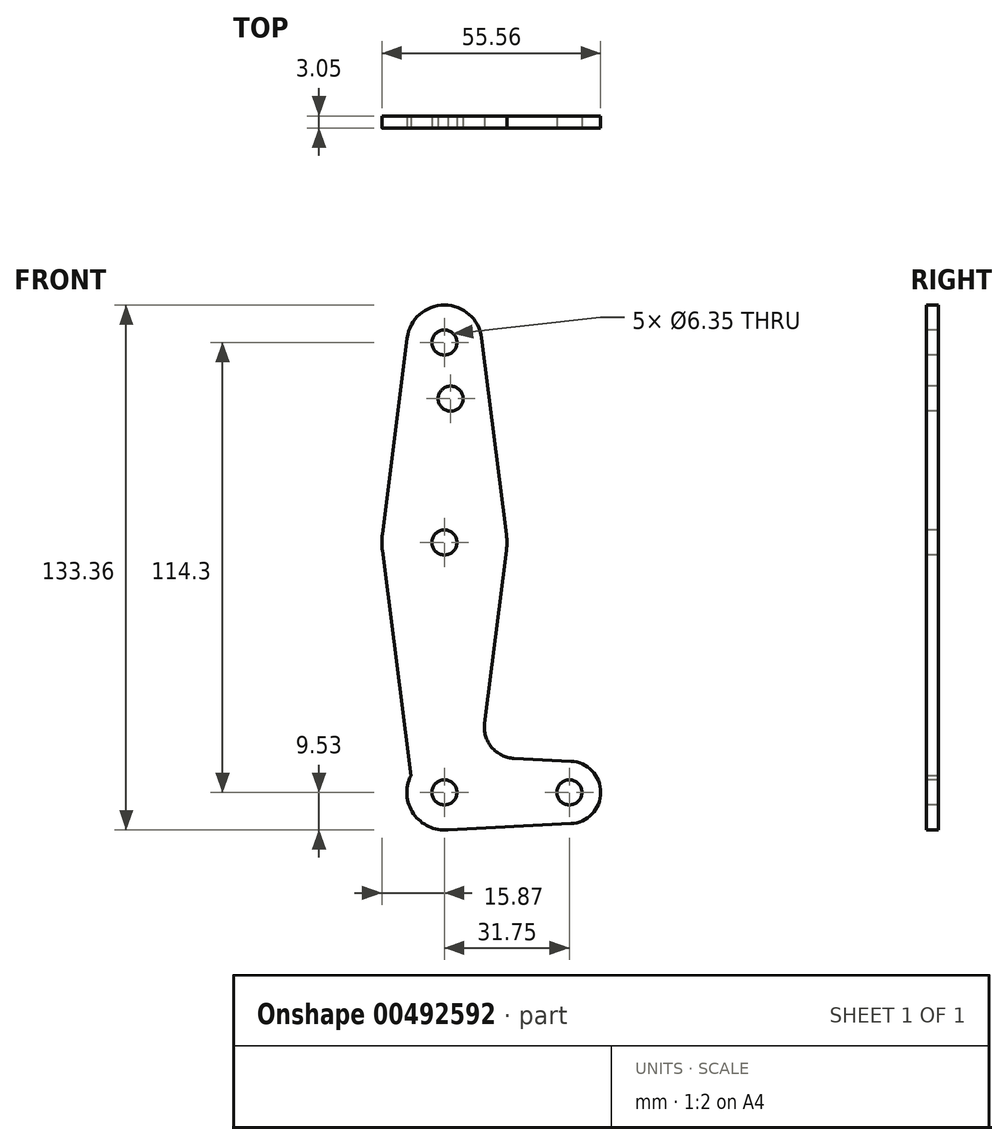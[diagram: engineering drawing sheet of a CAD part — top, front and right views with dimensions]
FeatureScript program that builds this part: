
annotation { "Feature Type Name" : "Feature", "Feature Type Description" : "" }
export const myFeature = defineFeature(function(context is Context, id is Id, definition is map)
    precondition{}
    {
        {
            var Q0;
            Q0=qCreatedBy(makeId("Front.planeOp"),FACE);
            var sketch = newSketch(context, id + "F0", { "sketchPlane" : qUnion([Q0])});
            skLineSegment(sketch, "E0", {"start": v(0, 0) * mm, "end": v(0, 114.3) * mm, "construction": true});
            skLineSegment(sketch, "E1", {"start": v(0, 0) * mm, "end": v(31.75, 0) * mm, "construction": true});
            skCircle(sketch, "E2", {"center": v(0, 114.3) * mm, "radius": 9.52 * mm});
            skCircle(sketch, "E3", {"center": v(0, 0) * mm, "radius": 9.53 * mm});
            skCircle(sketch, "E4", {"center": v(31.75, 0) * mm, "radius": 7.94 * mm});
            skCircle(sketch, "E5", {"center": v(0, 63.5) * mm, "radius": 15.88 * mm});
            skLineSegment(sketch, "E6", {"start": v(-9.45, 115.5) * mm, "end": v(-15.75, 65.48) * mm});
            skLineSegment(sketch, "E7", {"start": v(9.45, 115.5) * mm, "end": v(15.75, 65.48) * mm});
            skLineSegment(sketch, "E8", {"start": v(-15.75, 61.52) * mm, "end": v(-8, 0) * mm});
            skCircle(sketch, "E9", {"center": v(0, 114.3) * mm, "radius": 3.18 * mm});
            skCircle(sketch, "E10", {"center": v(0, 63.5) * mm, "radius": 3.18 * mm});
            skCircle(sketch, "E11", {"center": v(0, 0) * mm, "radius": 3.17 * mm});
            skCircle(sketch, "E12", {"center": v(31.75, 0) * mm, "radius": 3.18 * mm});
            skCircle(sketch, "E13", {"center": v(1.59, 100.03) * mm, "radius": 3.18 * mm});
            skLineSegment(sketch, "E14", {"start": v(15.75, 61.52) * mm, "end": v(10.22, 17.58) * mm});
            skLineSegment(sketch, "E15", {"start": v(17.7, 8.65) * mm, "end": v(32.14, 7.93) * mm});
            skLineSegment(sketch, "E16", {"start": v(0, -9.52) * mm, "end": v(32.14, -7.93) * mm});
            skArc(sketch, "E17.filletArc", {"start": v(10.22, 17.58) * mm, "mid": v(12.01, 11.48) * mm, "end": v(17.7, 8.65) * mm});
            skSolve(sketch);
        }
        {
            var Q0;
            Q0 = qSketchRegion(id + "F0", true);
            extrude(context, id + "F1", {"entities" : qUnion([Q0]), "oppositeDirection" : true, "depth" : 3.05 * mm});
        }
    });
